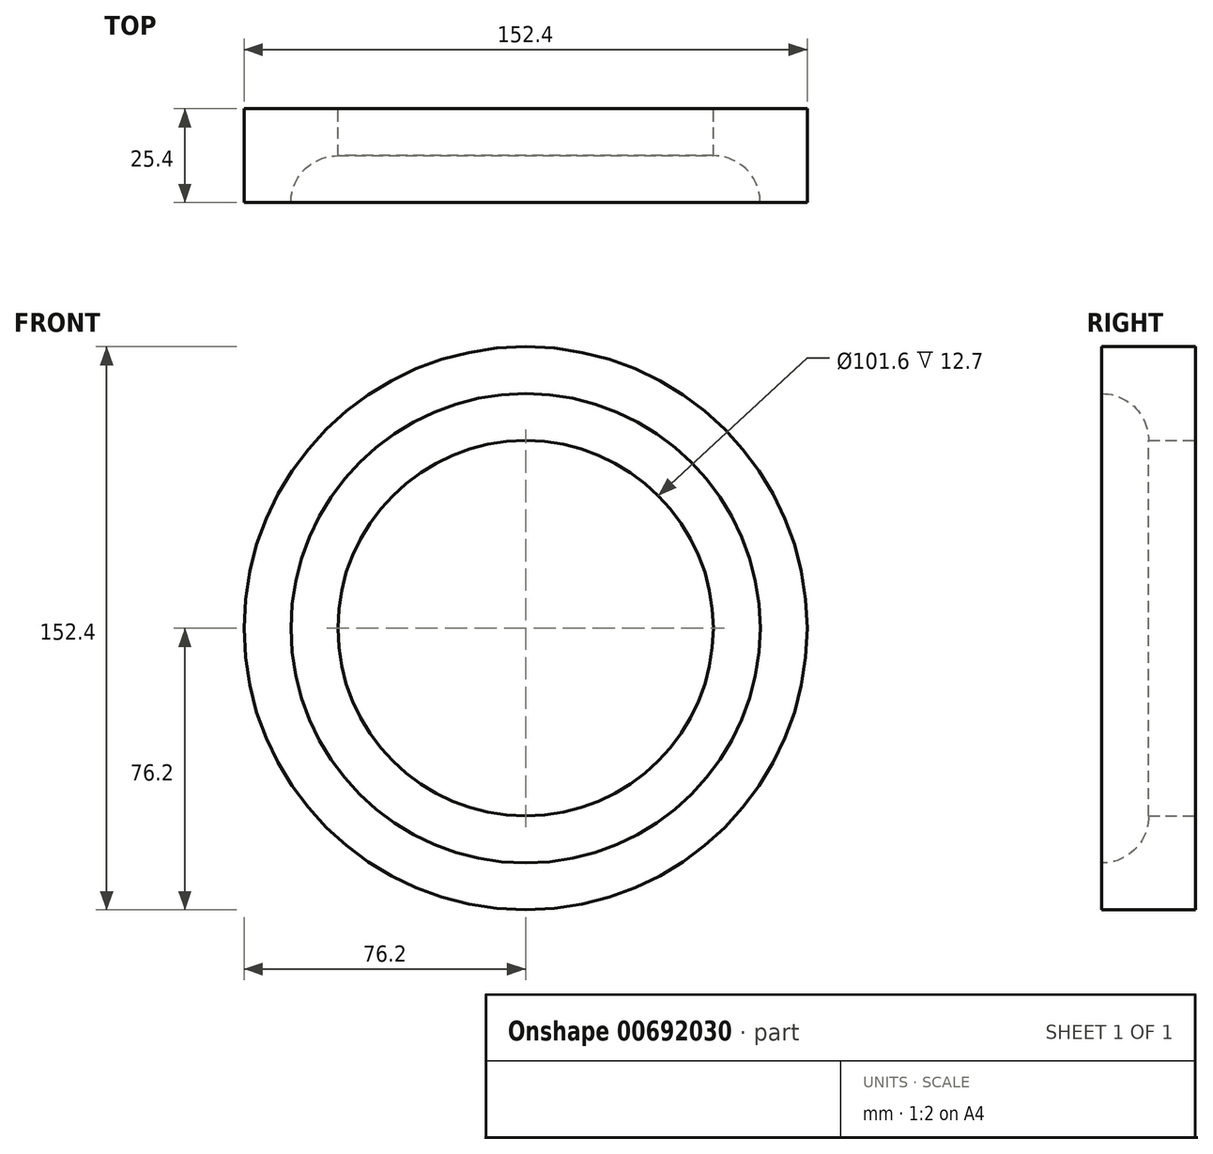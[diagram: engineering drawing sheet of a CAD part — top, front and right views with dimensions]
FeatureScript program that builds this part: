
annotation { "Feature Type Name" : "Feature", "Feature Type Description" : "" }
export const myFeature = defineFeature(function(context is Context, id is Id, definition is map)
    precondition{}
    {
        {
            var Q0;
            Q0=qCreatedBy(makeId("Front.planeOp"),FACE);
            var sketch = newSketch(context, id + "F0", { "sketchPlane" : qUnion([Q0])});
            skCircle(sketch, "E0", {"center": v(0, 0) * mm, "radius": 76.2 * mm});
            skCircle(sketch, "E1", {"center": v(0, 0) * mm, "radius": 50.8 * mm});
            skLineSegment(sketch, "E2", {"start": v(-50.8, 16.44) * mm, "end": v(-50.8, -14.53) * mm, "construction": true});
            skSolve(sketch);
        }
        {
            var Q0;
            Q0=makeQuery(id+"F0.imprint","IMPRINT",FACE,{"disambiguationData":[TD([[makeQuery(id+"F0.imprint","IMPRINT",EDGE,{"derivedFrom":sQuery(id+"F0.wireOp",EDGE,"E0")}),1.0]])]});
            extrude(context, id + "F1", {"entities" : qUnion([Q0]), "depth" : 25.4 * mm, "offsetDistance" : 25.4 * mm});
        }
        {
            var Q0;
            Q0=qCreatedBy(makeId("Top.planeOp"),FACE);
            var sketch = newSketch(context, id + "F2", { "sketchPlane" : qUnion([Q0])});
            skCircle(sketch, "E3", {"center": v(-50.8, -25.4) * mm, "radius": 12.7 * mm});
            skLineSegment(sketch, "E4", {"start": v(50.8, 0) * mm, "end": v(50.8, -25.4) * mm});
            skLineSegment(sketch, "E5", {"start": v(-50.8, -25.4) * mm, "end": v(-50.8, 0) * mm});
            skLineSegment(sketch, "E6", {"start": v(0, 17.87) * mm, "end": v(0, -41.02) * mm, "construction": true});
            skSolve(sketch);
        }
        {
            var Q0;
            Q0=makeQuery(id+"F2.imprint","IMPRINT",FACE,{"disambiguationData":[TD([[makeQuery(id+"F2.imprint","IMPRINT",EDGE,{"derivedFrom":sQuery(id+"F2.wireOp",EDGE,"E3")}),1.0]])]});
            var Q1;
            Q1=sQuery(id+"F2.wireOp",EDGE,"E6");
            revolve(context, id + "F3", {"operationType" : NewBodyOperationType.REMOVE, "entities" : qUnion([Q0]), "axis" : qUnion([Q1]), "revolveType" : RevolveType.FULL, "oppositeDirection" : true});
        }
    });
